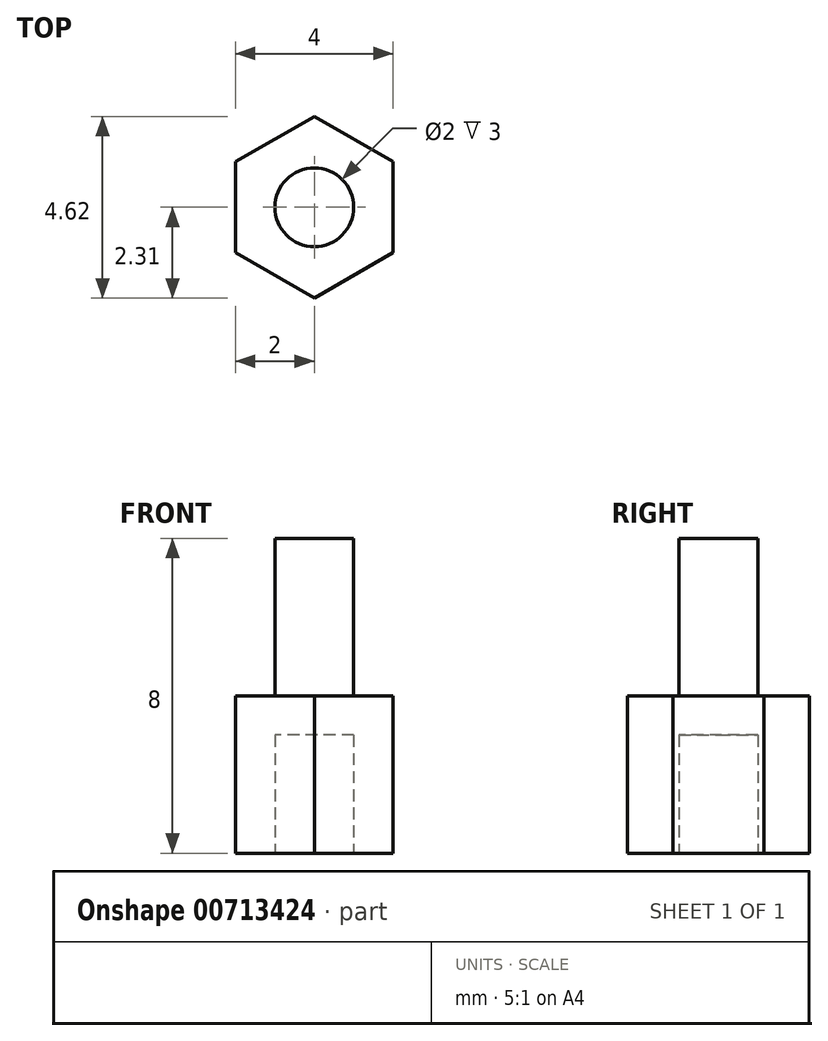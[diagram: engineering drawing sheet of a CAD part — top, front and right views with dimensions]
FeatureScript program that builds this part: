
annotation { "Feature Type Name" : "Feature", "Feature Type Description" : "" }
export const myFeature = defineFeature(function(context is Context, id is Id, definition is map)
    precondition{}
    {
        {
            var Q0;
            Q0=qCreatedBy(makeId("Top.planeOp"),FACE);
            var sketch = newSketch(context, id + "F0", { "sketchPlane" : qUnion([Q0])});
            skCircle(sketch, "E0.cCircle", {"center": v(0, 0) * mm, "radius": 2 * mm, "construction": true});
            skLineSegment(sketch, "E0.0", {"start": v(-2, -1.15) * mm, "end": v(-2, 1.15) * mm});
            skLineSegment(sketch, "E0.1", {"start": v(-2, 1.15) * mm, "end": v(0, 2.3) * mm});
            skLineSegment(sketch, "E0.2", {"start": v(0, 2.3) * mm, "end": v(2, 1.15) * mm});
            skLineSegment(sketch, "E0.3", {"start": v(2, 1.15) * mm, "end": v(2, -1.15) * mm});
            skLineSegment(sketch, "E0.4", {"start": v(2, -1.15) * mm, "end": v(0, -2.3) * mm});
            skLineSegment(sketch, "E0.5", {"start": v(0, -2.3) * mm, "end": v(-2, -1.15) * mm});
            skPoint(sketch, "E0.0.midPoint", {"position": v(-2, 0) * mm});
            skCircle(sketch, "E1", {"center": v(0, 0) * mm, "radius": 1 * mm});
            skSolve(sketch);
        }
        {
            var Q0;
            Q0=makeQuery(id+"F0.imprint","IMPRINT",FACE,{"disambiguationData":[TD([[makeQuery(id+"F0.imprint","IMPRINT",EDGE,{"derivedFrom":sQuery(id+"F0.wireOp",EDGE,"E0.0")}),-1.0]])]});
            extrude(context, id + "F1", {"entities" : qUnion([Q0]), "depth" : 4 * mm, "offsetDistance" : 25 * mm});
        }
        {
            var Q0;
            Q0=makeQuery(id+"F0.imprint","IMPRINT",FACE,{"disambiguationData":[TD([[makeQuery(id+"F0.imprint","IMPRINT",EDGE,{"derivedFrom":sQuery(id+"F0.wireOp",EDGE,"E1")}),1.0]])]});
            extrude(context, id + "F2", {"entities" : qUnion([Q0]), "operationType" : NewBodyOperationType.ADD, "depth" : 8 * mm, "offsetDistance" : 25 * mm, "hasSecondDirection" : true, "secondDirectionOppositeDirection" : false, "secondDirectionDepth" : 3 * mm});
        }
    });
